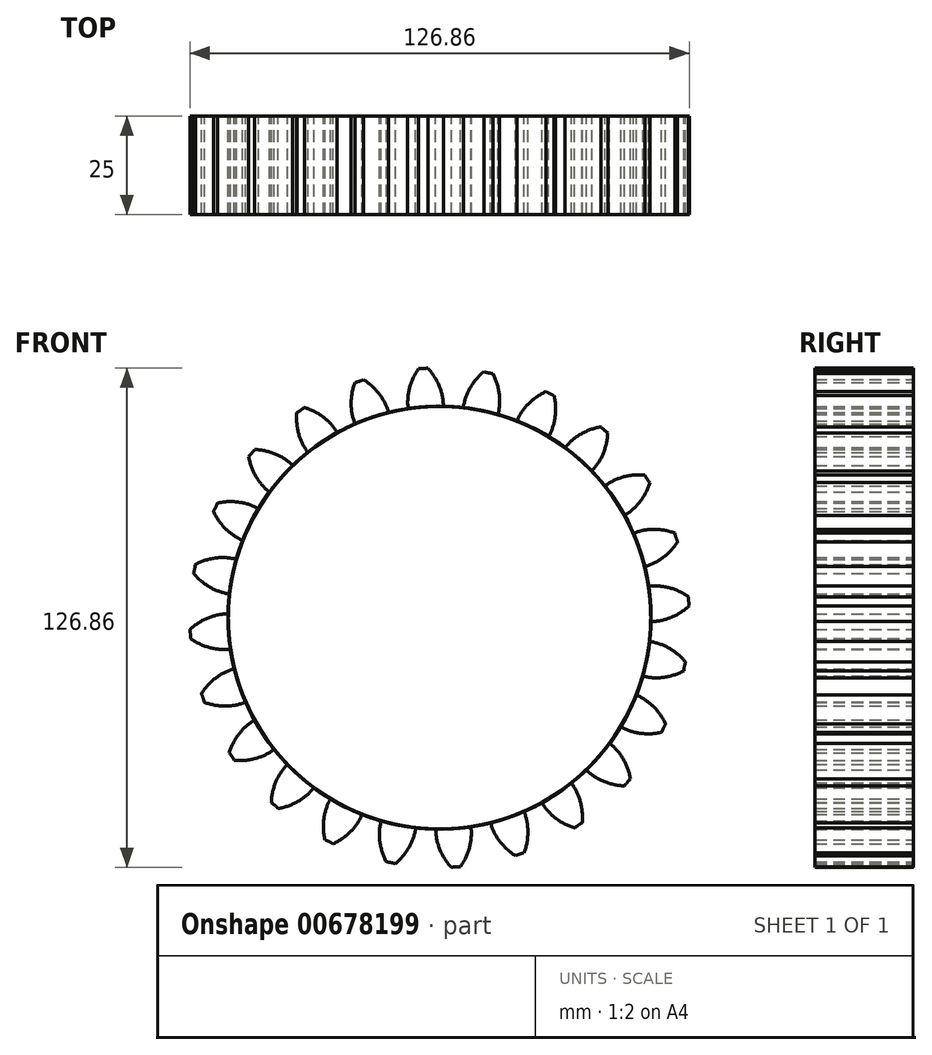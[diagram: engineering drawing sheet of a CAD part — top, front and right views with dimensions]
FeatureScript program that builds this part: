
annotation { "Feature Type Name" : "Feature", "Feature Type Description" : "" }
export const myFeature = defineFeature(function(context is Context, id is Id, definition is map)
    precondition{}
    {
        {
            var Q0;
            Q0=qCreatedBy(makeId("Front.planeOp"),FACE);
            var sketch = newSketch(context, id + "F0", { "sketchPlane" : qUnion([Q0])});
            skCircle(sketch, "E0", {"center": v(0, 0) * mm, "radius": 58.67 * mm, "construction": true});
            skCircle(sketch, "E1", {"center": v(0, 0) * mm, "radius": 63.5 * mm, "construction": true});
            skCircle(sketch, "E2", {"center": v(0, 0) * mm, "radius": 53.72 * mm});
            skLineSegment(sketch, "E3", {"start": v(0, 0) * mm, "end": v(0, 96.8) * mm, "construction": true});
            skLineSegment(sketch, "E4", {"start": v(0, 0) * mm, "end": v(-6.42, 97.88) * mm, "construction": true});
            skLineSegment(sketch, "E5", {"start": v(0, 58.67) * mm, "end": v(-73.18, 58.67) * mm, "construction": true});
            skLineSegment(sketch, "E6", {"start": v(0, 58.67) * mm, "end": v(-72.56, 32.26) * mm, "construction": true});
            skCircle(sketch, "E7", {"center": v(0, 0) * mm, "radius": 55.14 * mm, "construction": true});
            skCircle(sketch, "E8", {"center": v(0, 58.67) * mm, "radius": 14.6 * mm, "construction": true});
            skCircle(sketch, "E9", {"center": v(-13.63, 53.42) * mm, "radius": 14.6 * mm, "construction": true});
            skArc(sketch, "E10", {"start": v(0, 58.67) * mm, "mid": v(-1.28, 61.19) * mm, "end": v(-2.99, 63.43) * mm});
            skArc(sketch, "E11", {"start": v(0.97, 53.71) * mm, "mid": v(0.72, 56.24) * mm, "end": v(0, 58.67) * mm});
            skArc(sketch, "E12.MirrorCS", {"start": v(-7.66, 58.17) * mm, "mid": v(-6.72, 60.83) * mm, "end": v(-5.32, 63.28) * mm});
            skArc(sketch, "E13.MirrorCS", {"start": v(-7.98, 53.13) * mm, "mid": v(-8.05, 55.66) * mm, "end": v(-7.66, 58.17) * mm});
            skArc(sketch, "E14", {"start": v(-5.32, 63.28) * mm, "mid": v(-4.15, 63.3) * mm, "end": v(-2.99, 63.43) * mm});
            skSolve(sketch);
        }
        {
            var Q0;
            {var subQ0=sQuery(id+"F0.wireOp",EDGE,"E2");var subQ1=makeQuery(id+"F0.imprint","INTERSECT",VERTEX,{"derivedFrom":[subQ0,sQuery(id+"F0.wireOp",EDGE,"E11")]});Q0=makeQuery(id+"F0.imprint","IMPRINT",FACE,{"disambiguationData":[TD([[makeQuery(id+"F0.imprint","IMPRINT",EDGE,{"disambiguationData":[TD([[subQ1,-1.0]])],"derivedFrom":subQ0}),1.0]])]});}
            var Q1;
            Q1=makeQuery(id+"F0.imprint","IMPRINT",FACE,{"disambiguationData":[TD([[makeQuery(id+"F0.imprint","IMPRINT",EDGE,{"derivedFrom":sQuery(id+"F0.wireOp",EDGE,"E10")}),1.0]])]});
            extrude(context, id + "F1", {"entities" : qUnion([Q0, Q1]), "depth" : 25 * mm, "offsetDistance" : 25 * mm});
        }
        {
            var Q0;
            Q0=makeQuery(id+"F1.opExtrude","SWEPT_BODY",BODY,{"disambiguationData":[OSD([sQuery(id+"F0.wireOp",EDGE,"E2"),sQuery(id+"F0.wireOp",EDGE,"E10"),sQuery(id+"F0.wireOp",EDGE,"E11"),sQuery(id+"F0.wireOp",EDGE,"E12.MirrorCS"),sQuery(id+"F0.wireOp",EDGE,"E13.MirrorCS"),sQuery(id+"F0.wireOp",EDGE,"E14")])]});
            var Q1;
            Q1=makeQuery(id+"F1.opExtrude","SWEPT_FACE",FACE,{"disambiguationData":[OSD([sQuery(id+"F0.wireOp",EDGE,"E2")])]});
            circularPattern(context, id + "F2", {"entities" : qUnion([Q0]), "axis" : qUnion([Q1]), "angle" : 360 * degree, "instanceCount" : 24, "equalSpace" : true});
        }
    });
